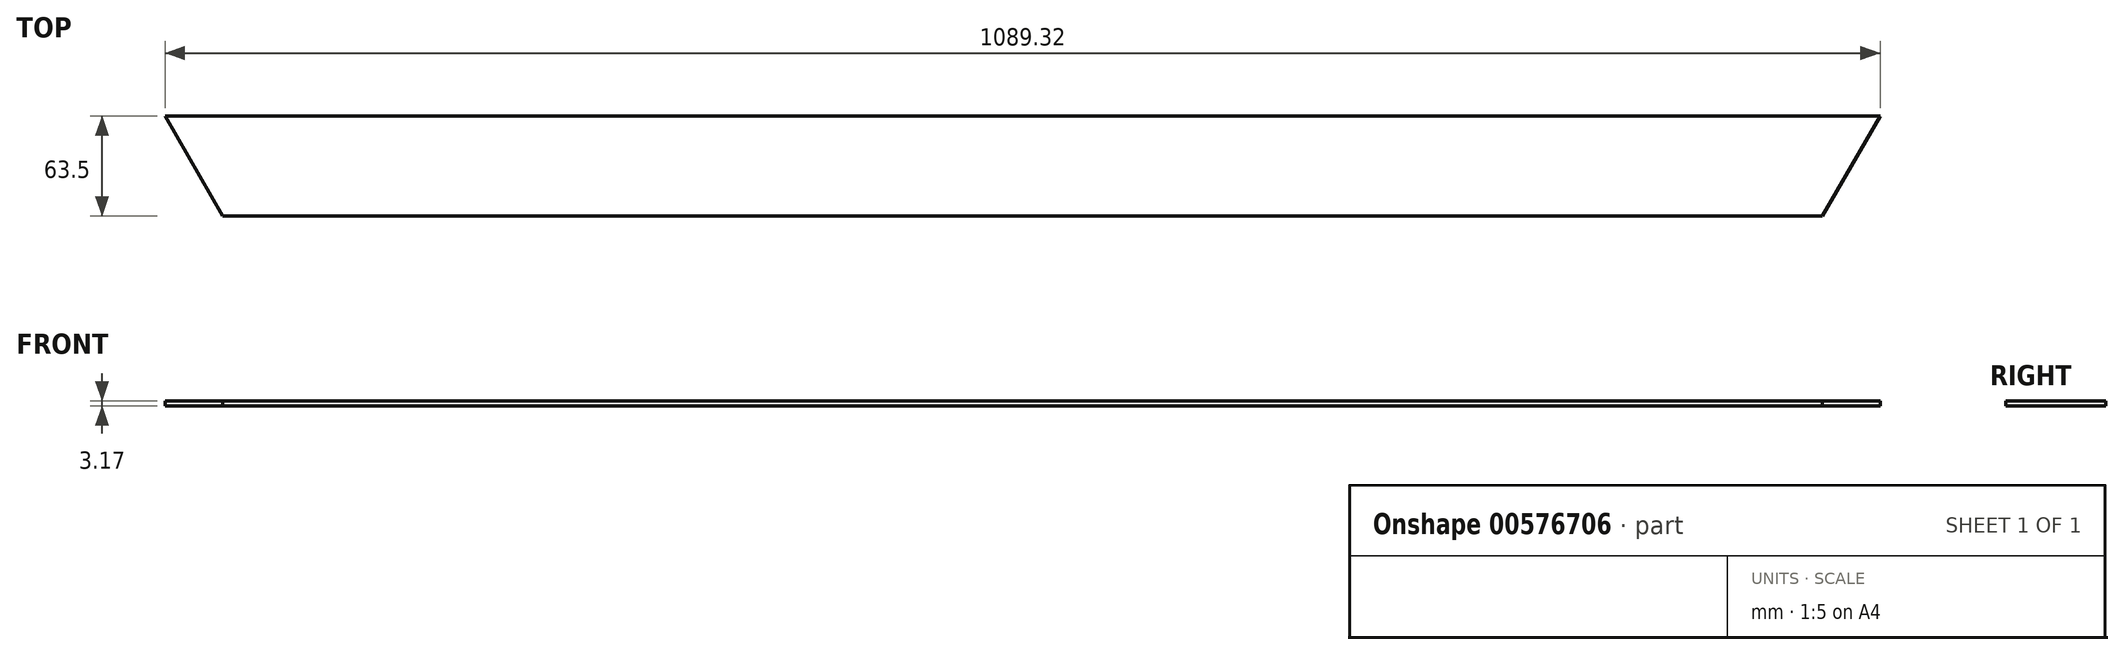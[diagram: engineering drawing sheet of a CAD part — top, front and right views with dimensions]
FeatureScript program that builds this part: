
annotation { "Feature Type Name" : "Feature", "Feature Type Description" : "" }
export const myFeature = defineFeature(function(context is Context, id is Id, definition is map)
    precondition{}
    {
        {
            var Q0;
            Q0=qCreatedBy(makeId("Top.planeOp"),FACE);
            var sketch = newSketch(context, id + "F0", { "sketchPlane" : qUnion([Q0])});
            skLineSegment(sketch, "E0.bottom", {"start": v(508, 31.75) * mm, "end": v(-508, 31.75) * mm});
            skLineSegment(sketch, "E0.top", {"start": v(508, -31.75) * mm, "end": v(-508, -31.75) * mm});
            skLineSegment(sketch, "E0.left", {"start": v(508, 31.75) * mm, "end": v(508, -31.75) * mm});
            skLineSegment(sketch, "E0.right", {"start": v(-508, 31.75) * mm, "end": v(-508, -31.75) * mm});
            skPoint(sketch, "E0.middle", {"position": v(0, 0) * mm});
            skLineSegment(sketch, "E1", {"start": v(508, 31.75) * mm, "end": v(544.66, 31.75) * mm});
            skLineSegment(sketch, "E2", {"start": v(-544.66, 31.75) * mm, "end": v(-508, 31.75) * mm});
            skLineSegment(sketch, "E3", {"start": v(544.66, 31.75) * mm, "end": v(508, -31.75) * mm});
            skLineSegment(sketch, "E4", {"start": v(-544.66, 31.75) * mm, "end": v(-508, -31.75) * mm});
            skSolve(sketch);
        }
        {
            var Q0;
            Q0 = qSketchRegion(id + "F0", true);
            extrude(context, id + "F1", {"entities" : qUnion([Q0]), "depth" : 3.17 * mm, "offsetDistance" : 25.4 * mm});
        }
    });
